# Revit family: JAD_Neon_A5582_BIM_DE
name_source: partatom
category: Plumbing Fixtures
revit_build: Autodesk Revit MEP 2016 (Build: 20161004_0715(x64)
units: mm (PartAtom-declared; Revit-internal decimal feet)

## family parameters
Always vertical = No
Cut with Voids When Loaded = No
Part Type = Normal
Room Calculation Point = No
Round Connector Dimension = Use Diameter
Shared = No
Work Plane-Based = No

## types (1)
- A5582AA NEON single lever one hole basin mixer, no pop-up waste
    Accessories = www.idealstandard.de\ersatzteile
    BOSUseNativeGeometries = 1
    Brand = Ideal Standard
    Brand url = http://www.idealstandard.de
    Date of publishing = 20/12/2017
    Edition number = 1
    InletConnectionSize = 0 mm  [stored 0 ft]
    Manufacturer name = Ideal standard test account
    ManufacturerURL = http://www.idealstandard.de
    Model = A5582AA
    Nominal height = 0
    Nominal width = 0
    NominalDepth = 0 mm  [stored 0 ft]
    NominalHeight = 302 mm
    NominalLength = 204 mm
    NominalWidth = 49 mm
    Product Guid = 455ebaee-b76d-4949-b940-950fabdad2db
    Product SKU = A5582AA
    Product data url = https://bimobject.com
    Product name = IS JADO Einhebel-Waschtischbatterie NEON ohne Ablaufgarnitur G1 1/4 Chrom
    ProductInformation = www.idealstandard.de/produkte
    QR code = http://bimobject.com
    Size = 49x204x302 mm
    URL = http://www.idealstandard.de
    Weight Net (Kg) = 0

note: [stored X ft] marks values corroborated as IEEE doubles in the binary element streams (Revit-internal decimal feet)

## geometry (parser evidence)
native form markers: Blend x4
no freeform markers — native parametric forms only
